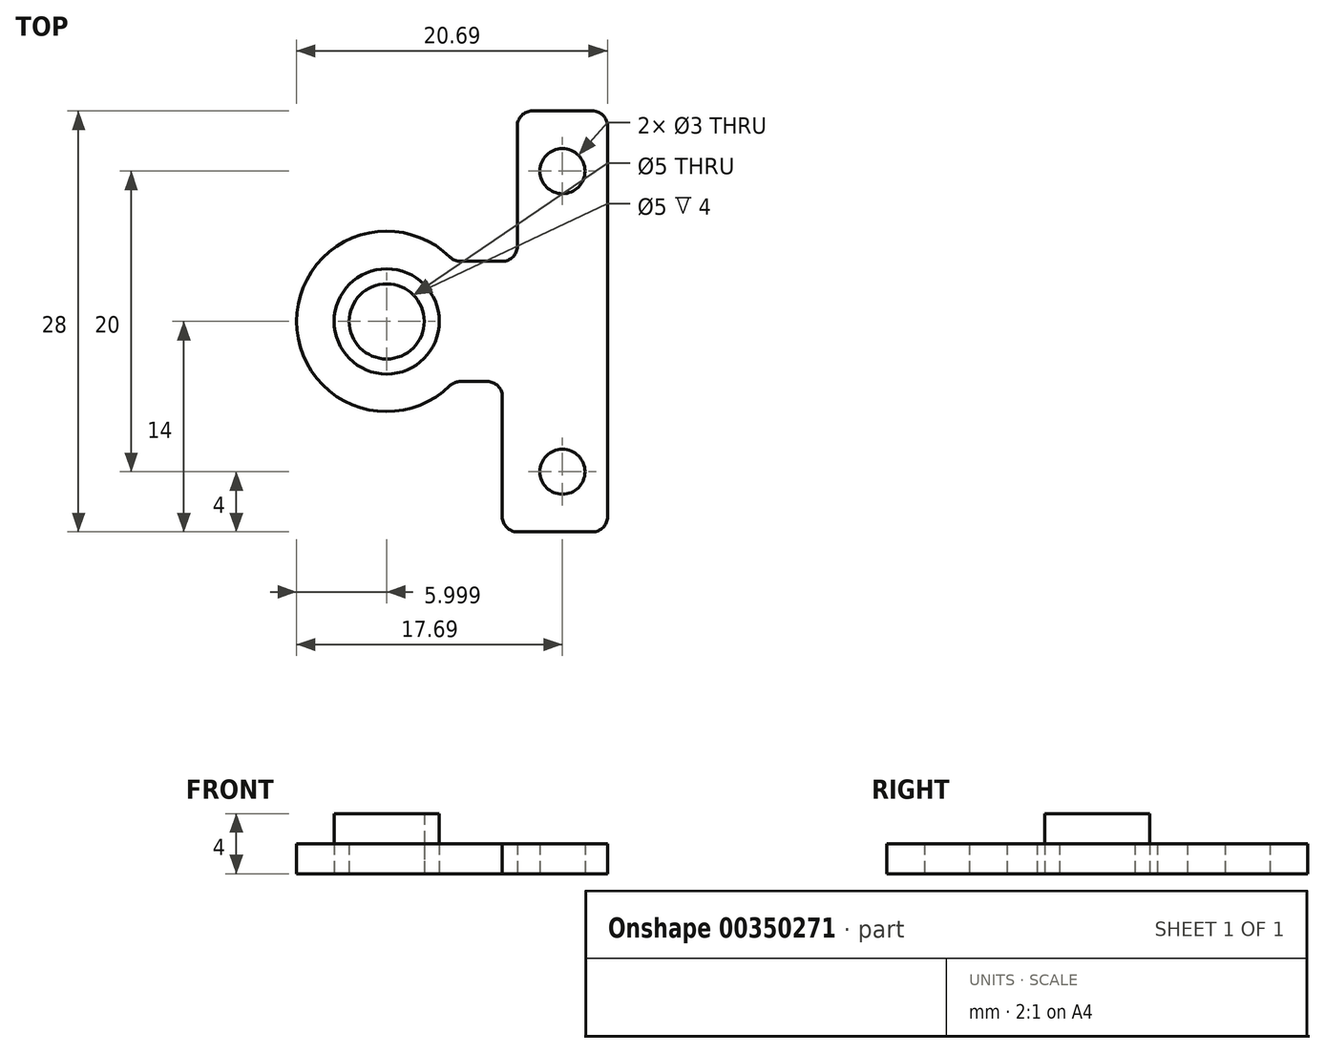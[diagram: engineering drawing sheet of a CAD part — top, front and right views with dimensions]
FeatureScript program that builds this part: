
annotation { "Feature Type Name" : "Feature", "Feature Type Description" : "" }
export const myFeature = defineFeature(function(context is Context, id is Id, definition is map)
    precondition{}
    {
        {
            var Q0;
            Q0=qCreatedBy(makeId("Top.planeOp"),FACE);
            var sketch = newSketch(context, id + "F0", { "sketchPlane" : qUnion([Q0])});
            skCircle(sketch, "E0", {"center": v(0, 10) * mm, "radius": 1.5 * mm});
            skCircle(sketch, "E1", {"center": v(0, -10) * mm, "radius": 1.5 * mm});
            skLineSegment(sketch, "E2.bottom", {"start": v(-2, 14) * mm, "end": v(2, 14) * mm});
            skLineSegment(sketch, "E2.top", {"start": v(-3, -14) * mm, "end": v(2, -14) * mm});
            skLineSegment(sketch, "E2.right", {"start": v(3, 13) * mm, "end": v(3, -13) * mm});
            skLineSegment(sketch, "E3.bottom", {"start": v(-6.8, 4) * mm, "end": v(-4, 4) * mm});
            skLineSegment(sketch, "E3.top", {"start": v(-6.8, -4) * mm, "end": v(-5, -4) * mm});
            skCircle(sketch, "E4", {"center": v(-11.7, 0) * mm, "radius": 2.5 * mm});
            skArc(sketch, "E5", {"start": v(-7.5, 4.29) * mm, "mid": v(-17.7, 0) * mm, "end": v(-7.5, -4.29) * mm});
            skLineSegment(sketch, "E6.trimOffspring", {"start": v(-4, -5) * mm, "end": v(-4, -13) * mm});
            skLineSegment(sketch, "E7", {"start": v(-3, 5) * mm, "end": v(-3, 13) * mm});
            skPoint(sketch, "E8.visualSharp", {"position": v(-3, 14) * mm});
            skArc(sketch, "E8.filletArc", {"start": v(-2, 14) * mm, "mid": v(-2.7, 13.7) * mm, "end": v(-3, 13) * mm});
            skPoint(sketch, "E9.visualSharp", {"position": v(3, 14) * mm});
            skArc(sketch, "E9.filletArc", {"start": v(3, 13) * mm, "mid": v(2.7, 13.7) * mm, "end": v(2, 14) * mm});
            skPoint(sketch, "E10.visualSharp", {"position": v(3, -14) * mm});
            skArc(sketch, "E10.filletArc", {"start": v(2, -14) * mm, "mid": v(2.7, -13.7) * mm, "end": v(3, -13) * mm});
            skPoint(sketch, "E11.visualSharp", {"position": v(-4, -14) * mm});
            skArc(sketch, "E11.filletArc", {"start": v(-4, -13) * mm, "mid": v(-3.7, -13.7) * mm, "end": v(-3, -14) * mm});
            skPoint(sketch, "E12.visualSharp", {"position": v(-4, -4) * mm});
            skArc(sketch, "E12.filletArc", {"start": v(-4, -5) * mm, "mid": v(-4.3, -4.3) * mm, "end": v(-5, -4) * mm});
            skPoint(sketch, "E13.visualSharp", {"position": v(-3, 4) * mm});
            skArc(sketch, "E13.filletArc", {"start": v(-4, 4) * mm, "mid": v(-3.3, 4.3) * mm, "end": v(-3, 5) * mm});
            skPoint(sketch, "E14.visualSharp", {"position": v(-7.22, 4) * mm});
            skArc(sketch, "E14.filletArc", {"start": v(-7.5, 4.29) * mm, "mid": v(-7.17, 4.07) * mm, "end": v(-6.8, 4) * mm});
            skPoint(sketch, "E15.visualSharp", {"position": v(-7.22, -4) * mm});
            skArc(sketch, "E15.filletArc", {"start": v(-6.8, -4) * mm, "mid": v(-7.17, -4.07) * mm, "end": v(-7.5, -4.29) * mm});
            skCircle(sketch, "E16", {"center": v(-11.7, 0) * mm, "radius": 3.5 * mm});
            skSolve(sketch);
        }
        {
            var Q0;
            Q0=makeQuery(id+"F0.imprint","IMPRINT",FACE,{"disambiguationData":[TD([[makeQuery(id+"F0.imprint","IMPRINT",EDGE,{"derivedFrom":sQuery(id+"F0.wireOp",EDGE,"E4")}),-1.0]])]});
            var Q1;
            Q1=sQuery(id+"F0.wireOp",EDGE,"E4");
            var Q2;
            Q2=sQuery(id+"F0.wireOp",EDGE,"E16");
            extrude(context, id + "F1", {"entities" : qUnion([Q0]), "surfaceEntities" : qUnion([Q1, Q2]), "depth" : 4 * mm});
        }
        {
            var Q0;
            Q0 = qSketchRegion(id + "F0", true);
            var Q1;
            Q1=makeQuery(id+"F0.imprint","IMPRINT",FACE,{"disambiguationData":[TD([[makeQuery(id+"F0.imprint","IMPRINT",EDGE,{"derivedFrom":sQuery(id+"F0.wireOp",EDGE,"E4")}),-1.0]])]});
            extrude(context, id + "F2", {"entities" : qUnion([Q0, Q1]), "depth" : 2 * mm});
        }
    });
